# Revit family: Graypants_Scraplights_Classics_Alki_Allyn_Denny_Madison_Pendant_R21_0925
name_source: partatom
category: Lighting Fixtures
units: mm (PartAtom-declared; Revit-internal decimal feet)

## family parameters
Cut with Voids When Loaded = No
Host = Face
Light Source = Yes
Part Type = Normal
Room Calculation Point = No
Round Connector Dimension = Use Diameter
Shared = No

## types (4) — shared parameters
Color Filter = 16777215
Default Elevation = 4' - 0"
Dimming Lamp Color Temperature Shift = <None>
Graypants_Cord/Canopy_Finish_Options = White | Black
Graypants_Manufacturer = Graypants
Graypants_Shade_Finish_Options = Natural Cardboard | Blonde Cardboard | White Cardboard
Graypants_URL = www.graypants.com
Light Source Symbol Size = 2' - 0"

## per-type parameters (varying)
| type | Graypants_Alki_Canopy_Visible | Graypants_Alki_Cord_Visible | Graypants_Alki_Shade_Visible | Graypants_Allyn_Canopy_Visible | Graypants_Allyn_Cord_Visible | Graypants_Allyn_Shade_Visible | Graypants_Denny_Canopy_Visible | Graypants_Denny_Cord_Visible | Graypants_Denny_Shade_Visible | Graypants_Madison_Canopy_Visible | Graypants_Madison_Cord_Visible | Graypants_Madison_Shade_Visible | Graypants_Model |
| Graypants_Scraplights_Alki_Pendant | Yes | Yes | Yes | No | No | No | No | No | No | No | No | No | Scraplights_Classics_Alki |
| Graypants_Scraplights_Allyn_Pendant | No | No | No | Yes | Yes | Yes | No | No | No | No | No | No | Scraplights_Classics_Allyn |
| Graypants_Scraplights_Denny_Pendant | No | No | No | No | No | No | Yes | Yes | Yes | No | No | No | Scraplights_Classics_Denny |
| Graypants_Scraplights_Madison_Pendant | No | No | No | No | No | No | No | No | No | Yes | Yes | Yes | Scraplights_Classics_Madison |

## geometry (parser evidence)
native form markers: Sweep x12
no freeform markers — native parametric forms only
